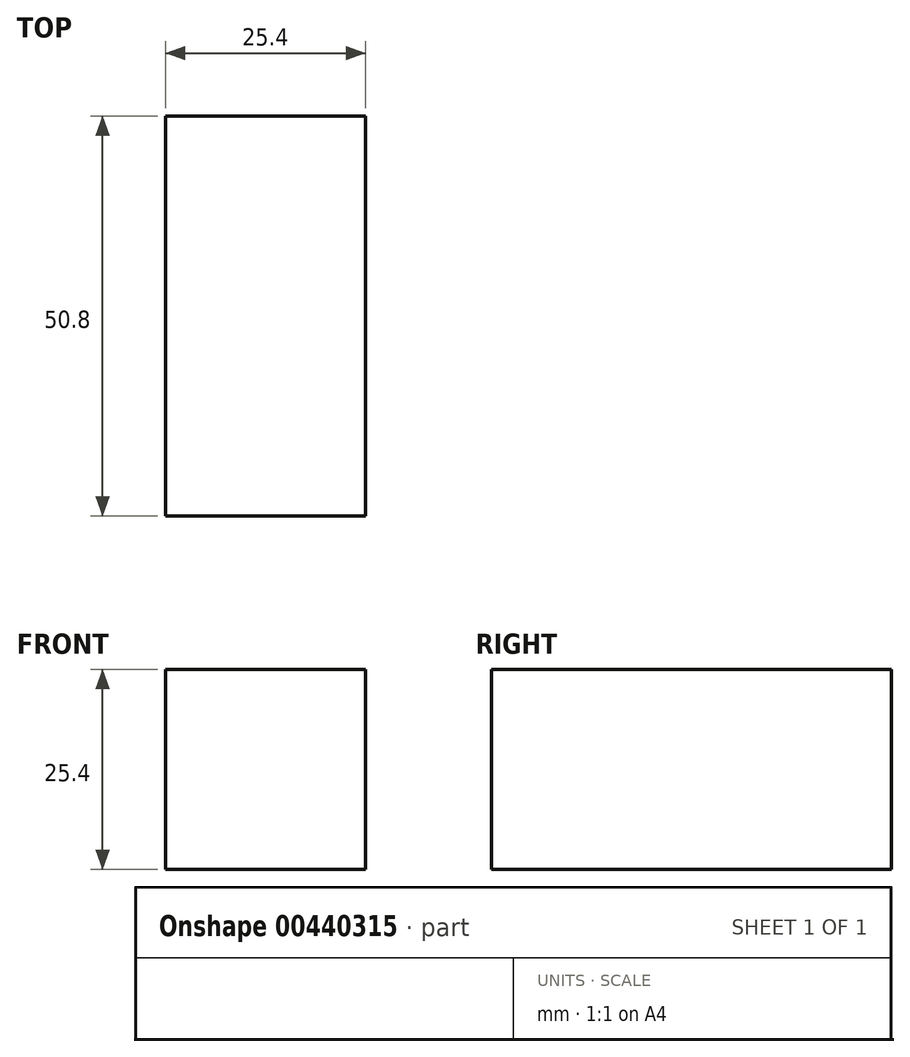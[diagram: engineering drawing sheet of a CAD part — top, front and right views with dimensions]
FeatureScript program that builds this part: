
annotation { "Feature Type Name" : "Feature", "Feature Type Description" : "" }
export const myFeature = defineFeature(function(context is Context, id is Id, definition is map)
    precondition{}
    {
        {
            var Q0;
            Q0=qCreatedBy(makeId("Front.planeOp"),FACE);
            var sketch = newSketch(context, id + "F0", { "sketchPlane" : qUnion([Q0])});
            skLineSegment(sketch, "E0.bottom", {"start": v(7.31, 0) * mm, "end": v(-18.09, 0) * mm});
            skLineSegment(sketch, "E0.top", {"start": v(7.31, 25.4) * mm, "end": v(-18.09, 25.4) * mm});
            skLineSegment(sketch, "E0.left", {"start": v(7.31, 0) * mm, "end": v(7.31, 25.4) * mm});
            skLineSegment(sketch, "E0.right", {"start": v(-18.09, 0) * mm, "end": v(-18.09, 25.4) * mm});
            skSolve(sketch);
        }
        {
            var Q0;
            Q0 = qSketchRegion(id + "F0", true);
            extrude(context, id + "F1", {"entities" : qUnion([Q0]), "depth" : 50.8 * mm});
        }
    });
